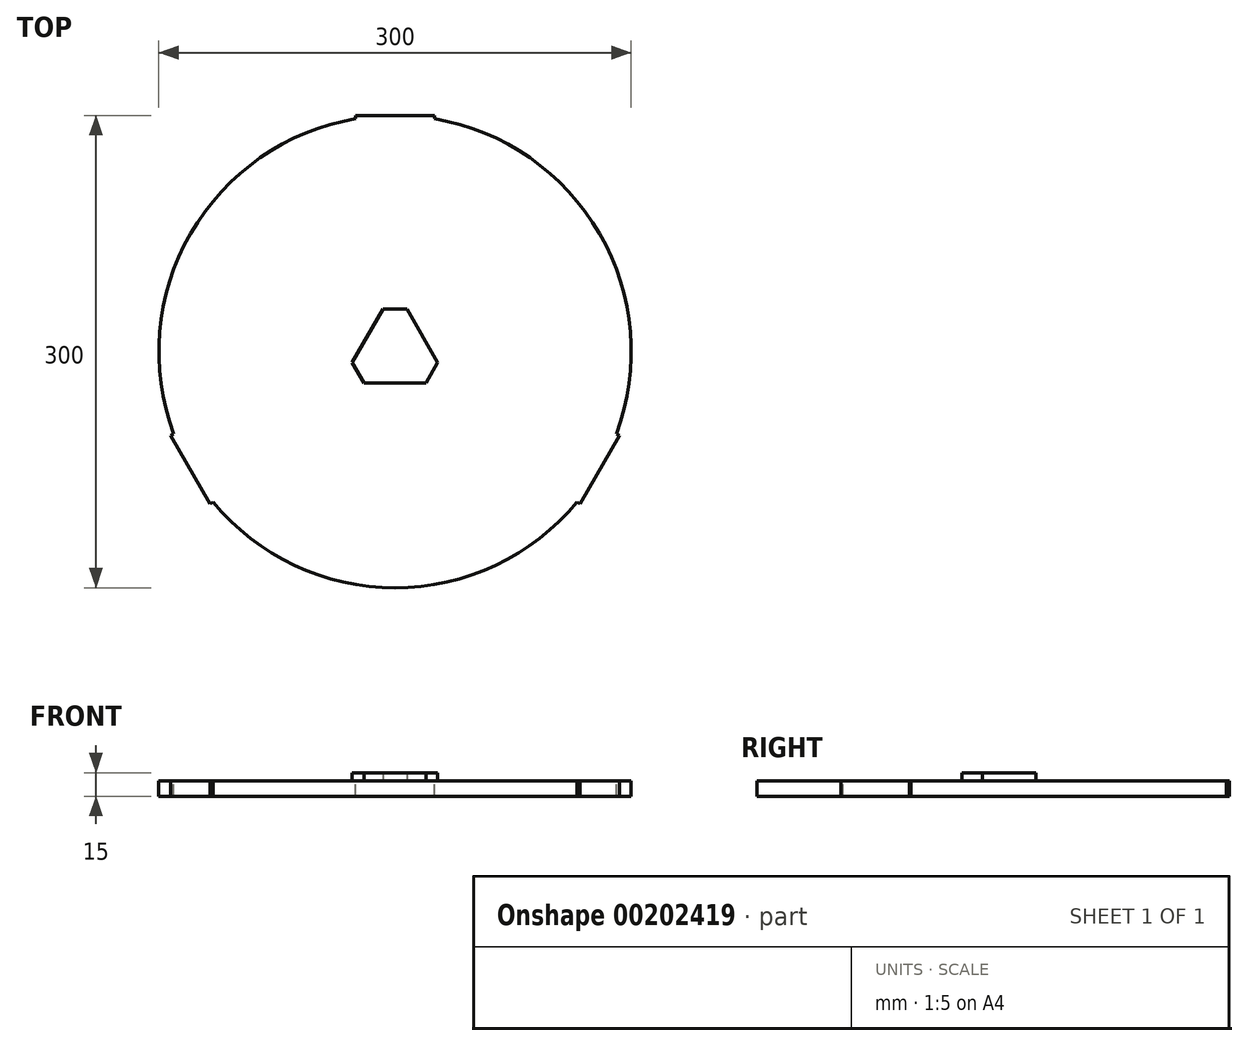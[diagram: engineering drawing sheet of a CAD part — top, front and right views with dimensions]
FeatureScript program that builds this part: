
annotation { "Feature Type Name" : "Feature", "Feature Type Description" : "" }
export const myFeature = defineFeature(function(context is Context, id is Id, definition is map)
    precondition{}
    {
        {
            var Q0;
            Q0=qCreatedBy(makeId("Top.planeOp"),FACE);
            var sketch = newSketch(context, id + "F0", { "sketchPlane" : qUnion([Q0])});
            skArc(sketch, "E0", {"start": v(-115.59, -95.6) * mm, "mid": v(0, -150) * mm, "end": v(115.59, -95.6) * mm});
            skLineSegment(sketch, "E1", {"start": v(0, 0) * mm, "end": v(0, 200.82) * mm, "construction": true});
            skPoint(sketch, "E2", {"position": v(0, 150) * mm});
            skPoint(sketch, "E3.1.0", {"position": v(-129.9, -75) * mm});
            skPoint(sketch, "E3.2.0", {"position": v(129.9, -75) * mm});
            skLineSegment(sketch, "E4", {"start": v(-129.9, -75) * mm, "end": v(-142.4, -53.35) * mm});
            skLineSegment(sketch, "E5", {"start": v(-129.9, -75) * mm, "end": v(-117.4, -96.65) * mm});
            skLineSegment(sketch, "E6", {"start": v(-142.4, -53.35) * mm, "end": v(-140.59, -52.3) * mm});
            skLineSegment(sketch, "E7", {"start": v(-117.4, -96.65) * mm, "end": v(-115.59, -95.6) * mm});
            skPoint(sketch, "E8", {"position": v(-140.59, -52.3) * mm});
            skLineSegment(sketch, "E9.1.0", {"start": v(129.9, -75) * mm, "end": v(142.4, -53.35) * mm});
            skLineSegment(sketch, "E9.1.1", {"start": v(129.9, -75) * mm, "end": v(117.4, -96.65) * mm});
            skLineSegment(sketch, "E9.1.2", {"start": v(117.4, -96.65) * mm, "end": v(115.59, -95.6) * mm});
            skLineSegment(sketch, "E9.1.3", {"start": v(142.4, -53.35) * mm, "end": v(140.59, -52.3) * mm});
            skLineSegment(sketch, "E9.2.0", {"start": v(0, 150) * mm, "end": v(-25, 150) * mm});
            skLineSegment(sketch, "E9.2.1", {"start": v(0, 150) * mm, "end": v(25, 150) * mm});
            skLineSegment(sketch, "E9.2.2", {"start": v(25, 150) * mm, "end": v(25, 147.9) * mm});
            skLineSegment(sketch, "E9.2.3", {"start": v(-25, 150) * mm, "end": v(-25, 147.9) * mm});
            skArc(sketch, "E10.trimOffspring", {"start": v(140.59, -52.3) * mm, "mid": v(129.9, 75) * mm, "end": v(25, 147.9) * mm});
            skArc(sketch, "E11.trimOffspring", {"start": v(-25, 147.9) * mm, "mid": v(-129.9, 75) * mm, "end": v(-140.59, -52.3) * mm});
            skSolve(sketch);
        }
        {
            var Q0;
            Q0=qSketchRegion(id+"F0",true);
            extrude(context, id + "F1", {"entities" : qUnion([Q0]), "oppositeDirection" : true, "depth" : 10 * mm});
        }
        {
            var Q0;
            Q0=qCreatedBy(makeId("Top.planeOp"),FACE);
            var sketch = newSketch(context, id + "F2", { "sketchPlane" : qUnion([Q0])});
            skCircle(sketch, "E12.cCircle", {"center": v(0, 0) * mm, "radius": 40 * mm, "construction": true});
            skLineSegment(sketch, "E12.0", {"start": v(7.5, 27) * mm, "end": v(27.14, -7) * mm});
            skLineSegment(sketch, "E12.1", {"start": v(19.64, -20) * mm, "end": v(-19.64, -20) * mm});
            skLineSegment(sketch, "E12.2", {"start": v(-27.14, -7) * mm, "end": v(-7.5, 27) * mm});
            skCircle(sketch, "E13.cCircle", {"center": v(0, 0) * mm, "radius": 54.02 * mm, "construction": true});
            skLineSegment(sketch, "E13.0", {"start": v(0, -54.02) * mm, "end": v(-8.64, -39.06) * mm});
            skLineSegment(sketch, "E13.1", {"start": v(-46.78, 27) * mm, "end": v(-29.5, 27) * mm});
            skLineSegment(sketch, "E13.2", {"start": v(46.78, 27) * mm, "end": v(38.14, 12.05) * mm});
            skPoint(sketch, "E14", {"position": v(27.14, -7) * mm});
            skPoint(sketch, "E15", {"position": v(19.64, -20) * mm});
            skPoint(sketch, "E16.orphan", {"position": v(0, 40) * mm});
            skLineSegment(sketch, "E17.trimOffspring", {"start": v(-7.5, 27) * mm, "end": v(7.5, 27) * mm});
            skLineSegment(sketch, "E18.trimOffspring", {"start": v(-38.14, 12.05) * mm, "end": v(-46.78, 27) * mm});
            skPoint(sketch, "E19.orphan", {"position": v(-34.64, -20) * mm});
            skLineSegment(sketch, "E20.trimOffspring", {"start": v(-19.64, -20) * mm, "end": v(-27.14, -7) * mm});
            skLineSegment(sketch, "E21.trimOffspring", {"start": v(8.64, -39.06) * mm, "end": v(0, -54.02) * mm});
            skLineSegment(sketch, "E22.trimOffspring", {"start": v(27.14, -7) * mm, "end": v(19.64, -20) * mm});
            skLineSegment(sketch, "E23.trimOffspring", {"start": v(29.5, 27) * mm, "end": v(46.78, 27) * mm});
            skPoint(sketch, "E24.orphan", {"position": v(34.64, -20) * mm});
            skSolve(sketch);
        }
        {
            var Q0;
            Q0=makeQuery(id+"F2.imprint","IMPRINT",FACE,{"disambiguationData":[TD([[makeQuery(id+"F2.imprint","IMPRINT",EDGE,{"derivedFrom":sQuery(id+"F2.wireOp",EDGE,"E12.0")}),-1.0]])]});
            extrude(context, id + "F3", {"entities" : qUnion([Q0]), "depth" : 5 * mm});
        }
    });
